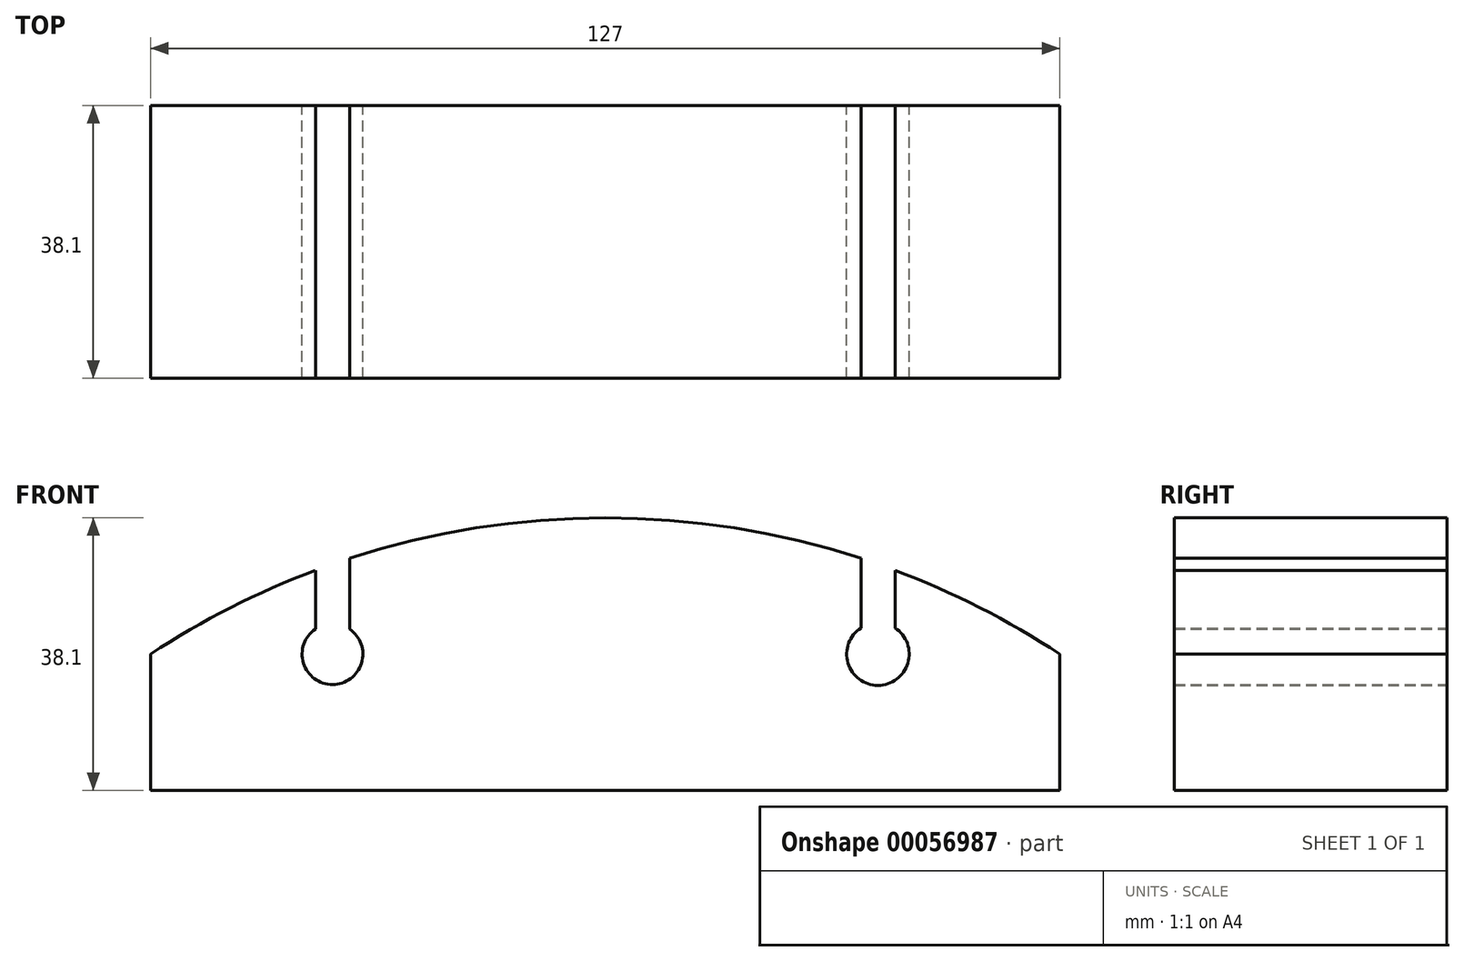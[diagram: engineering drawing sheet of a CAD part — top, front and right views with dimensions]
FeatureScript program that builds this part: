
annotation { "Feature Type Name" : "Feature", "Feature Type Description" : "" }
export const myFeature = defineFeature(function(context is Context, id is Id, definition is map)
    precondition{}
    {
        {
            var Q0;
            Q0=qCreatedBy(makeId("Front.planeOp"),FACE);
            var sketch = newSketch(context, id + "F0", { "sketchPlane" : qUnion([Q0])});
            skLineSegment(sketch, "E0.bottom", {"start": v(-63.3, -6) * mm, "end": v(63.7, -6) * mm});
            skLineSegment(sketch, "E0.left", {"start": v(-63.3, -6) * mm, "end": v(-63.3, 13.06) * mm});
            skLineSegment(sketch, "E0.right", {"start": v(63.7, -6) * mm, "end": v(63.7, 13.06) * mm});
            skArc(sketch, "E1", {"start": v(63.7, 13.06) * mm, "mid": v(52.53, 19.56) * mm, "end": v(40.7, 24.77) * mm});
            skArc(sketch, "E2", {"start": v(35.92, 16.71) * mm, "mid": v(38.3, 8.69) * mm, "end": v(40.7, 16.71) * mm});
            skArc(sketch, "E3", {"start": v(-40.28, 16.56) * mm, "mid": v(-37.9, 8.81) * mm, "end": v(-35.5, 16.56) * mm});
            skLineSegment(sketch, "E4", {"start": v(-40.28, 16.56) * mm, "end": v(-40.28, 24.77) * mm});
            skLineSegment(sketch, "E5", {"start": v(-35.5, 16.56) * mm, "end": v(-35.5, 26.44) * mm});
            skLineSegment(sketch, "E6", {"start": v(-35.5, 26.44) * mm, "end": v(-35.5, 23.9) * mm});
            skArc(sketch, "E7.trimOffspring", {"start": v(-40.28, 24.77) * mm, "mid": v(-52.12, 19.56) * mm, "end": v(-63.3, 13.06) * mm});
            skLineSegment(sketch, "E8", {"start": v(35.92, 16.71) * mm, "end": v(35.92, 26.44) * mm});
            skLineSegment(sketch, "E9", {"start": v(40.7, 16.71) * mm, "end": v(40.7, 24.77) * mm});
            skArc(sketch, "E10.trimOffspring", {"start": v(35.92, 26.44) * mm, "mid": v(0.2, 32.1) * mm, "end": v(-35.5, 26.44) * mm});
            skSolve(sketch);
        }
        {
            var Q0;
            Q0=makeQuery(id+"F0.imprint","IMPRINT",FACE,{"disambiguationData":[TD([[makeQuery(id+"F0.imprint","IMPRINT",EDGE,{"derivedFrom":sQuery(id+"F0.wireOp",EDGE,"E0.bottom")}),1.0]])]});
            extrude(context, id + "F1", {"entities" : qUnion([Q0]), "depth" : 38.1 * mm});
        }
    });
